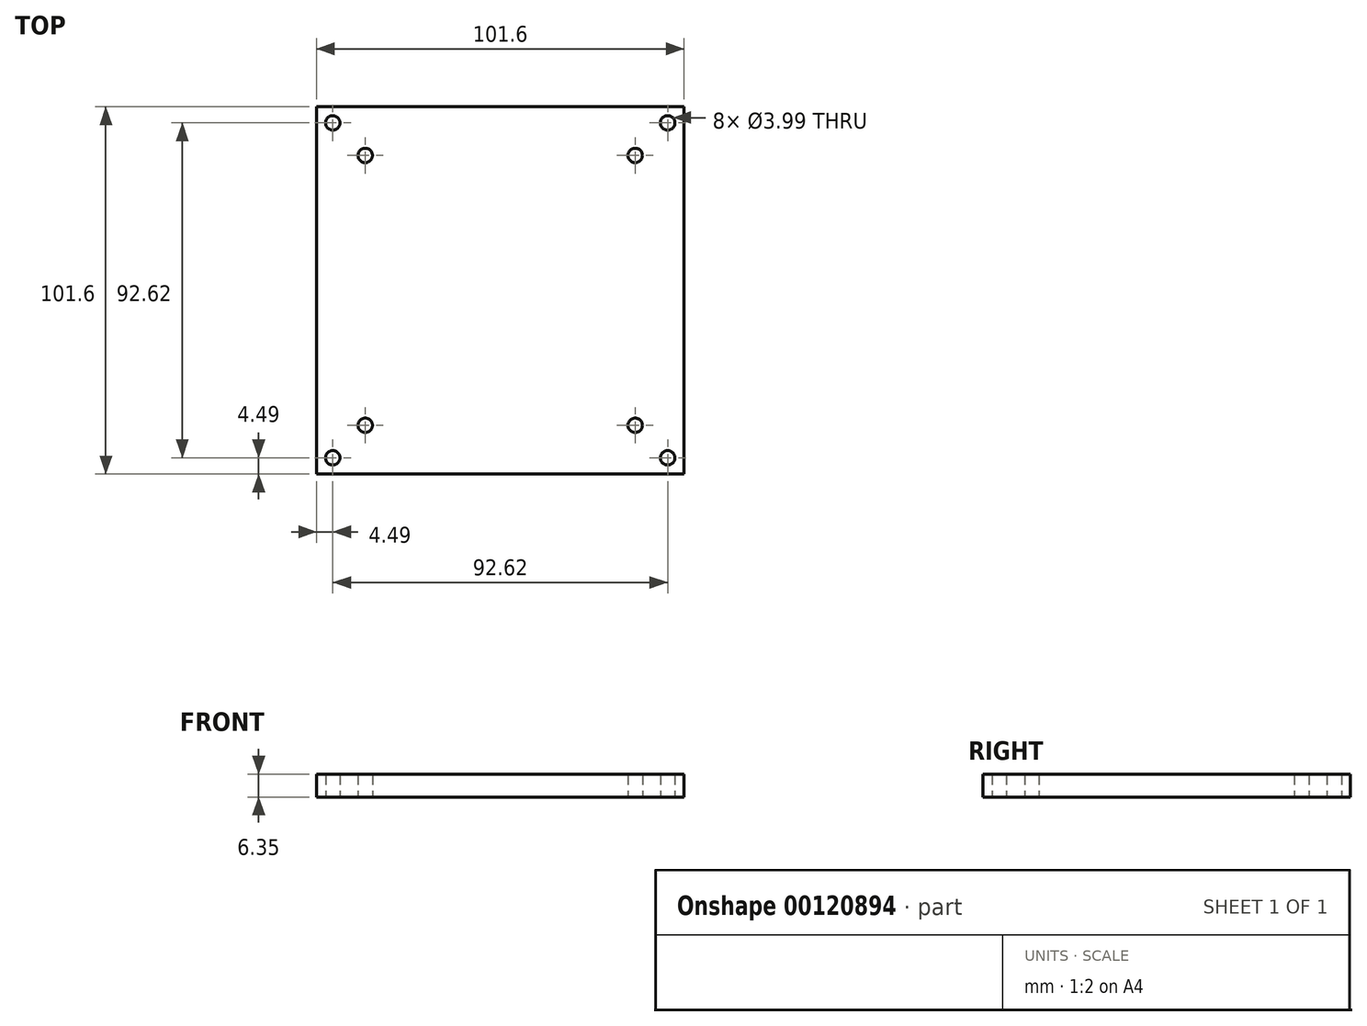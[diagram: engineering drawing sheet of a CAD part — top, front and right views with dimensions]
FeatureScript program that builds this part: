
annotation { "Feature Type Name" : "Feature", "Feature Type Description" : "" }
export const myFeature = defineFeature(function(context is Context, id is Id, definition is map)
    precondition{}
    {
        {
            var Q0;
            Q0=qCreatedBy(makeId("Top.planeOp"),FACE);
            var sketch = newSketch(context, id + "F0", { "sketchPlane" : qUnion([Q0])});
            skLineSegment(sketch, "E0.bottom", {"start": v(-50.8, 50.8) * mm, "end": v(50.8, 50.8) * mm});
            skLineSegment(sketch, "E0.top", {"start": v(-50.8, -50.8) * mm, "end": v(50.8, -50.8) * mm});
            skLineSegment(sketch, "E0.left", {"start": v(-50.8, 50.8) * mm, "end": v(-50.8, -50.8) * mm});
            skLineSegment(sketch, "E0.right", {"start": v(50.8, 50.8) * mm, "end": v(50.8, -50.8) * mm});
            skLineSegment(sketch, "E1", {"start": v(-50.8, 50.8) * mm, "end": v(50.8, -50.8) * mm, "construction": true});
            skLineSegment(sketch, "E2", {"start": v(-50.8, -50.8) * mm, "end": v(50.8, 50.8) * mm, "construction": true});
            skPoint(sketch, "E3", {"position": v(-46.3, 46.3) * mm});
            skPoint(sketch, "E4", {"position": v(-37.33, 37.33) * mm});
            skPoint(sketch, "E5.MirrorP", {"position": v(46.3, 46.3) * mm});
            skPoint(sketch, "E6.MirrorP", {"position": v(37.33, 37.33) * mm});
            skPoint(sketch, "E7.MirrorP", {"position": v(46.3, -46.3) * mm});
            skCircle(sketch, "E8", {"center": v(-46.3, 46.3) * mm, "radius": 2 * mm});
            skCircle(sketch, "E9", {"center": v(-37.33, 37.33) * mm, "radius": 2 * mm});
            skCircle(sketch, "E10.MirrorC", {"center": v(-37.33, -37.33) * mm, "radius": 2 * mm});
            skCircle(sketch, "E11.MirrorC", {"center": v(-46.3, -46.3) * mm, "radius": 2 * mm});
            skCircle(sketch, "E12.MirrorC", {"center": v(37.33, 37.33) * mm, "radius": 2 * mm});
            skCircle(sketch, "E13.MirrorC", {"center": v(46.3, 46.3) * mm, "radius": 2 * mm});
            skCircle(sketch, "E14.MirrorC", {"center": v(37.33, -37.33) * mm, "radius": 2 * mm});
            skCircle(sketch, "E15.MirrorC", {"center": v(46.3, -46.3) * mm, "radius": 2 * mm});
            skSolve(sketch);
        }
        {
            var Q0;
            Q0=makeQuery(id+"F0.imprint","IMPRINT",FACE,{"disambiguationData":[TD([[makeQuery(id+"F0.imprint","IMPRINT",EDGE,{"derivedFrom":sQuery(id+"F0.wireOp",EDGE,"E0.bottom")}),-1.0]])]});
            extrude(context, id + "F1", {"entities" : qUnion([Q0]), "depth" : 6.35 * mm});
        }
    });
